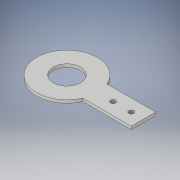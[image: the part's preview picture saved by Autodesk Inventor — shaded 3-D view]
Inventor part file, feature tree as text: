
AUTODESK INVENTOR PART (.ipt)
format: ipt  version: 2019 (Build 230136000, 136)  size: 113,152 bytes
history: native  units: in
note: dims shown in document units (in); Inventor stores cm internally (conversion verified against a paired STEP export)
features: extrude x1, sketch x1
ambient origin geometry x8: Origin, YZ Plane, XZ Plane, XY Plane, X Axis, Y Axis, Z Axis, Center Point
bodies: Solid1 (feature_tree)
feature tree (2):
  extrude  "Extrusion1"  Depth=0.5in
  sketch  "Sketch1"  dims[d0=0.5in d1=2.0in d5=0.5in d6=0.75in d7=0.2031in d8=0.2031in d9=1.125in d10=0.125in d11=0.0in d12=0.5in]
